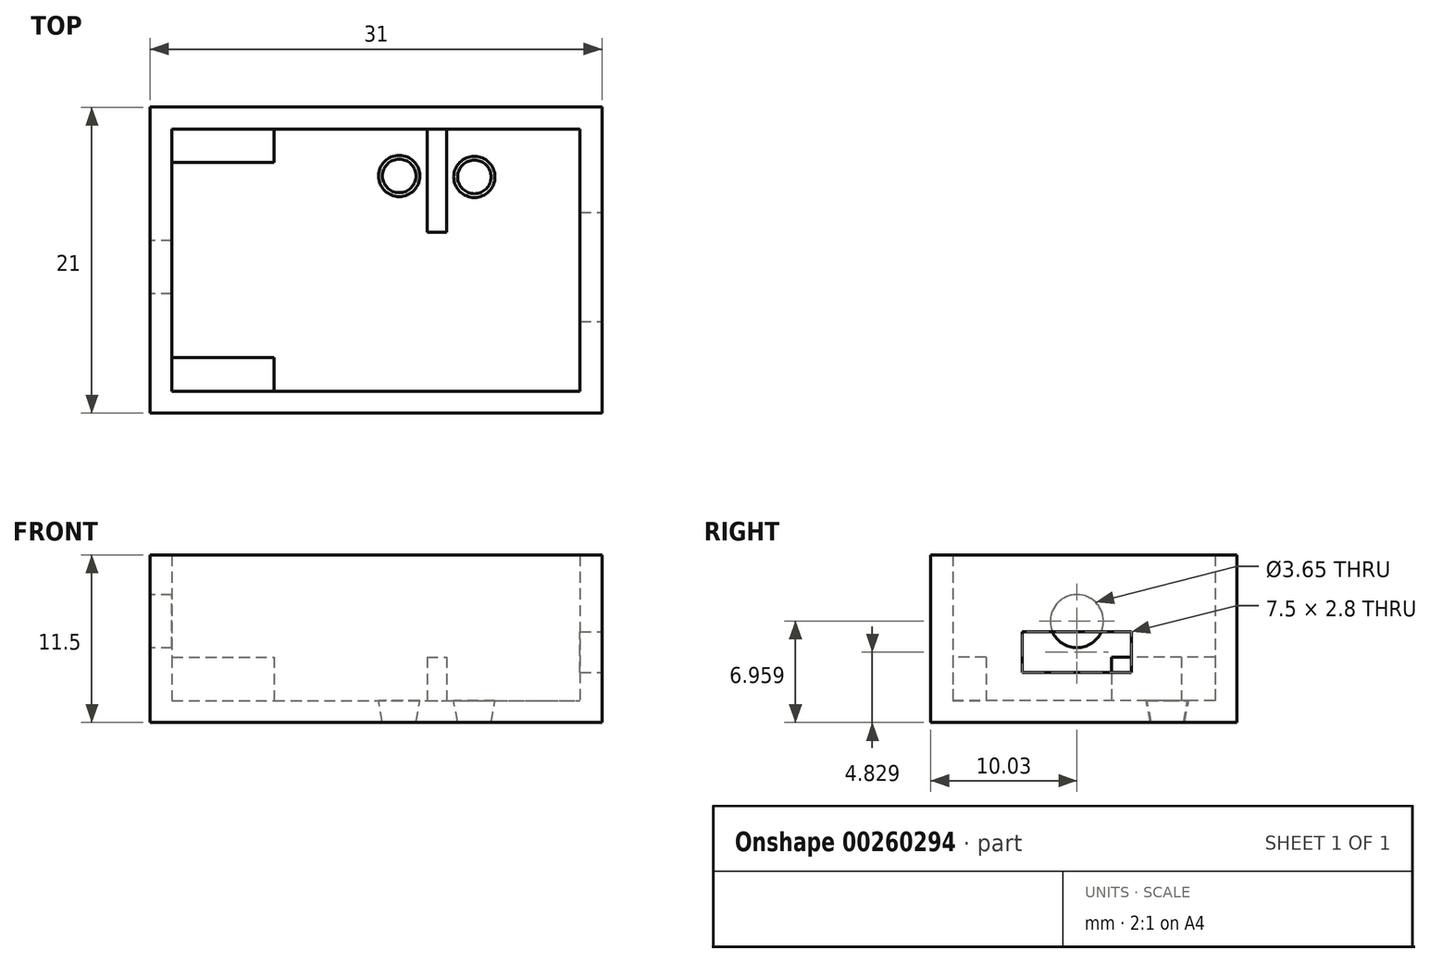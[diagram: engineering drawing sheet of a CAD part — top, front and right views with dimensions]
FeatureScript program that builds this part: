
annotation { "Feature Type Name" : "Feature", "Feature Type Description" : "" }
export const myFeature = defineFeature(function(context is Context, id is Id, definition is map)
    precondition{}
    {
        {
            var Q0;
            Q0=qCreatedBy(makeId("Top.planeOp"),FACE);
            var sketch = newSketch(context, id + "F0", { "sketchPlane" : qUnion([Q0])});
            skLineSegment(sketch, "E0.bottom", {"start": v(-16.97, 9.47) * mm, "end": v(11.03, 9.47) * mm});
            skLineSegment(sketch, "E0.top", {"start": v(-16.97, -8.53) * mm, "end": v(11.03, -8.53) * mm});
            skLineSegment(sketch, "E0.left", {"start": v(-16.97, 9.47) * mm, "end": v(-16.97, -8.53) * mm});
            skLineSegment(sketch, "E0.right", {"start": v(11.03, 9.47) * mm, "end": v(11.03, -8.53) * mm});
            skSolve(sketch);
        }
        {
            var Q0;
            Q0=makeQuery(id+"F0.imprint","IMPRINT",FACE,{"disambiguationData":[TD([[makeQuery(id+"F0.imprint","IMPRINT",EDGE,{"derivedFrom":sQuery(id+"F0.wireOp",EDGE,"E0.bottom")}),-1.0]])]});
            extrude(context, id + "F1", {"entities" : qUnion([Q0]), "depth" : 10 * mm});
        }
        {
            var Q0;
            Q0=makeQuery(id+"F1.opExtrude","CAP_FACE",FACE,{"disambiguationData":[OSD([sQuery(id+"F0.wireOp",EDGE,"E0.bottom"),sQuery(id+"F0.wireOp",EDGE,"E0.top"),sQuery(id+"F0.wireOp",EDGE,"E0.left"),sQuery(id+"F0.wireOp",EDGE,"E0.right")])],"isStart":false});
            var Q1;
            Q1=makeQuery(id+"F1.opExtrude","SWEPT_BODY",BODY,{"disambiguationData":[OSD([sQuery(id+"F0.wireOp",EDGE,"E0.bottom"),sQuery(id+"F0.wireOp",EDGE,"E0.top"),sQuery(id+"F0.wireOp",EDGE,"E0.left"),sQuery(id+"F0.wireOp",EDGE,"E0.right")])]});
            shell(context, id + "F2", {"entities" : qUnion([Q0]), "parts" : qUnion([Q1]), "thickness" : 1.5 * mm, "oppositeDirection" : true});
        }
        {
            var Q0;
            Q0=makeQuery(id+"F1.opExtrude","SWEPT_FACE",FACE,{"disambiguationData":[OSD([sQuery(id+"F0.wireOp",EDGE,"E0.right")])]});
            var sketch = newSketch(context, id + "F3", { "sketchPlane" : qUnion([Q0])});
            skLineSegment(sketch, "E1.bottom", {"start": v(3.75, 1.93) * mm, "end": v(-3.75, 1.93) * mm});
            skLineSegment(sketch, "E1.top", {"start": v(3.75, 4.73) * mm, "end": v(-3.75, 4.73) * mm});
            skLineSegment(sketch, "E1.left", {"start": v(3.75, 1.93) * mm, "end": v(3.75, 4.73) * mm});
            skLineSegment(sketch, "E1.right", {"start": v(-3.75, 1.93) * mm, "end": v(-3.75, 4.73) * mm});
            skPoint(sketch, "E1.middle", {"position": v(0, 3.33) * mm});
            skSolve(sketch);
        }
        {
            var Q0;
            Q0 = qSketchRegion(id + "F3", true);
            extrude(context, id + "F4", {"entities" : qUnion([Q0]), "operationType" : NewBodyOperationType.REMOVE, "oppositeDirection" : true, "depth" : 2 * mm});
        }
        {
            var Q0;
            Q0=makeQuery(id+"F1.opExtrude","CAP_FACE",FACE,{"disambiguationData":[OSD([sQuery(id+"F0.wireOp",EDGE,"E0.bottom"),sQuery(id+"F0.wireOp",EDGE,"E0.top"),sQuery(id+"F0.wireOp",EDGE,"E0.left"),sQuery(id+"F0.wireOp",EDGE,"E0.right")])],"isStart":true});
            var sketch = newSketch(context, id + "F5", { "sketchPlane" : qUnion([Q0])});
            skCircle(sketch, "E2", {"center": v(-1.38, -6.25) * mm, "radius": 1.15 * mm});
            skCircle(sketch, "E3", {"center": v(3.78, -6.18) * mm, "radius": 1.15 * mm});
            skSolve(sketch);
        }
        {
            var Q0;
            Q0 = qSketchRegion(id + "F5", true);
            extrude(context, id + "F6", {"entities" : qUnion([Q0]), "operationType" : NewBodyOperationType.REMOVE, "oppositeDirection" : true, "depth" : 3 * mm, "hasDraft" : true, "draftAngle" : 10 * degree});
        }
        {
            var Q0;
            Q0=makeQuery(id+"F2.opShell","OFFSET_FACE",FACE,{"disambiguationData":[OSD([sQuery(id+"F0.wireOp",EDGE,"E0.bottom"),sQuery(id+"F0.wireOp",EDGE,"E0.top"),sQuery(id+"F0.wireOp",EDGE,"E0.left"),sQuery(id+"F0.wireOp",EDGE,"E0.right")])]});
            var sketch = newSketch(context, id + "F7", { "sketchPlane" : qUnion([Q0])});
            skLineSegment(sketch, "E4.bottom", {"start": v(0.53, 9.47) * mm, "end": v(1.87, 9.47) * mm});
            skLineSegment(sketch, "E4.top", {"start": v(0.53, 2.38) * mm, "end": v(1.87, 2.38) * mm});
            skLineSegment(sketch, "E4.left", {"start": v(0.53, 9.47) * mm, "end": v(0.53, 2.38) * mm});
            skLineSegment(sketch, "E4.right", {"start": v(1.87, 9.47) * mm, "end": v(1.87, 2.38) * mm});
            skLineSegment(sketch, "E5.bottom", {"start": v(-16.97, -8.53) * mm, "end": v(-9.97, -8.53) * mm});
            skLineSegment(sketch, "E5.top", {"start": v(-16.97, -6.23) * mm, "end": v(-9.97, -6.23) * mm});
            skLineSegment(sketch, "E5.left", {"start": v(-16.97, -8.53) * mm, "end": v(-16.97, -6.23) * mm});
            skLineSegment(sketch, "E5.right", {"start": v(-9.97, -8.53) * mm, "end": v(-9.97, -6.23) * mm});
            skLineSegment(sketch, "E6.bottom", {"start": v(-16.97, 9.47) * mm, "end": v(-9.97, 9.47) * mm});
            skLineSegment(sketch, "E6.top", {"start": v(-16.97, 7.17) * mm, "end": v(-9.97, 7.17) * mm});
            skLineSegment(sketch, "E6.left", {"start": v(-16.97, 9.47) * mm, "end": v(-16.97, 7.17) * mm});
            skLineSegment(sketch, "E6.right", {"start": v(-9.97, 9.47) * mm, "end": v(-9.97, 7.17) * mm});
            skSolve(sketch);
        }
        {
            var Q0;
            Q0 = qSketchRegion(id + "F7", true);
            extrude(context, id + "F8", {"entities" : qUnion([Q0]), "operationType" : NewBodyOperationType.ADD, "depth" : 3 * mm});
        }
        {
            var Q0;
            Q0=makeQuery(id+"F1.opExtrude","SWEPT_FACE",FACE,{"disambiguationData":[OSD([sQuery(id+"F0.wireOp",EDGE,"E0.left")])]});
            var sketch = newSketch(context, id + "F9", { "sketchPlane" : qUnion([Q0])});
            skCircle(sketch, "E7", {"center": v(0, 5.46) * mm, "radius": 1.82 * mm});
            skSolve(sketch);
        }
        {
            var Q0;
            Q0 = qSketchRegion(id + "F9", true);
            extrude(context, id + "F10", {"entities" : qUnion([Q0]), "operationType" : NewBodyOperationType.REMOVE, "oppositeDirection" : true, "depth" : 5 * mm});
        }
    });
